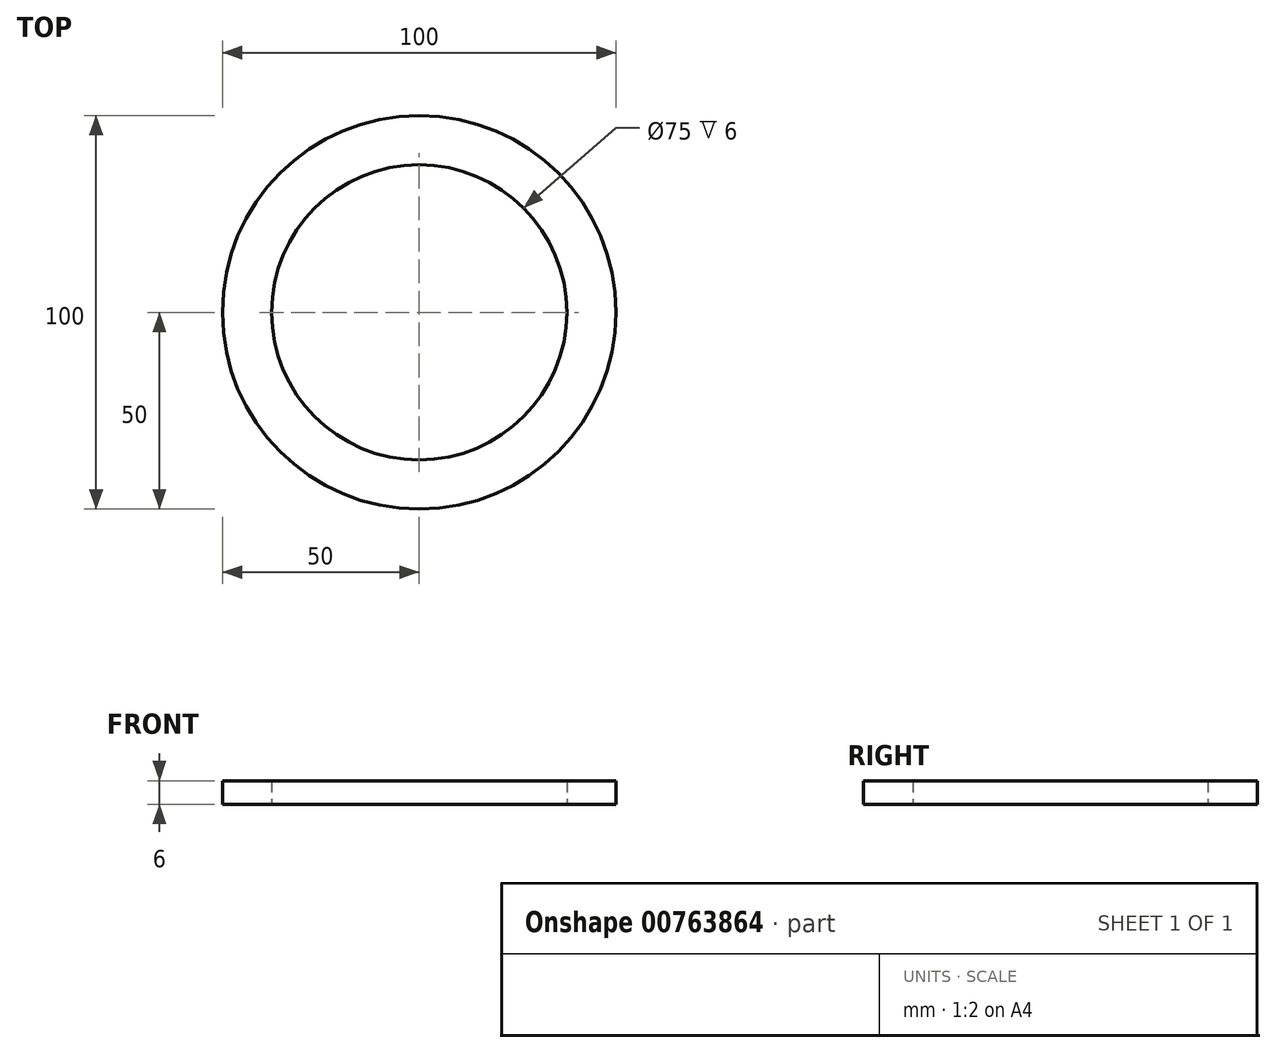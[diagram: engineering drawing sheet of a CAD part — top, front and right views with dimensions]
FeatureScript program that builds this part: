
annotation { "Feature Type Name" : "Feature", "Feature Type Description" : "" }
export const myFeature = defineFeature(function(context is Context, id is Id, definition is map)
    precondition{}
    {
        {
            var Q0;
            Q0=qCreatedBy(makeId("Top.planeOp"),FACE);
            var sketch = newSketch(context, id + "F0", { "sketchPlane" : qUnion([Q0])});
            skCircle(sketch, "E0", {"center": v(0, 0) * mm, "radius": 37.5 * mm});
            skCircle(sketch, "E1", {"center": v(0, 0) * mm, "radius": 50 * mm});
            skSolve(sketch);
        }
        {
            var Q0;
            Q0 = qSketchRegion(id + "F0", true);
            extrude(context, id + "F1", {"entities" : qUnion([Q0]), "depth" : 6 * mm, "offsetDistance" : 25.4 * mm});
        }
    });
